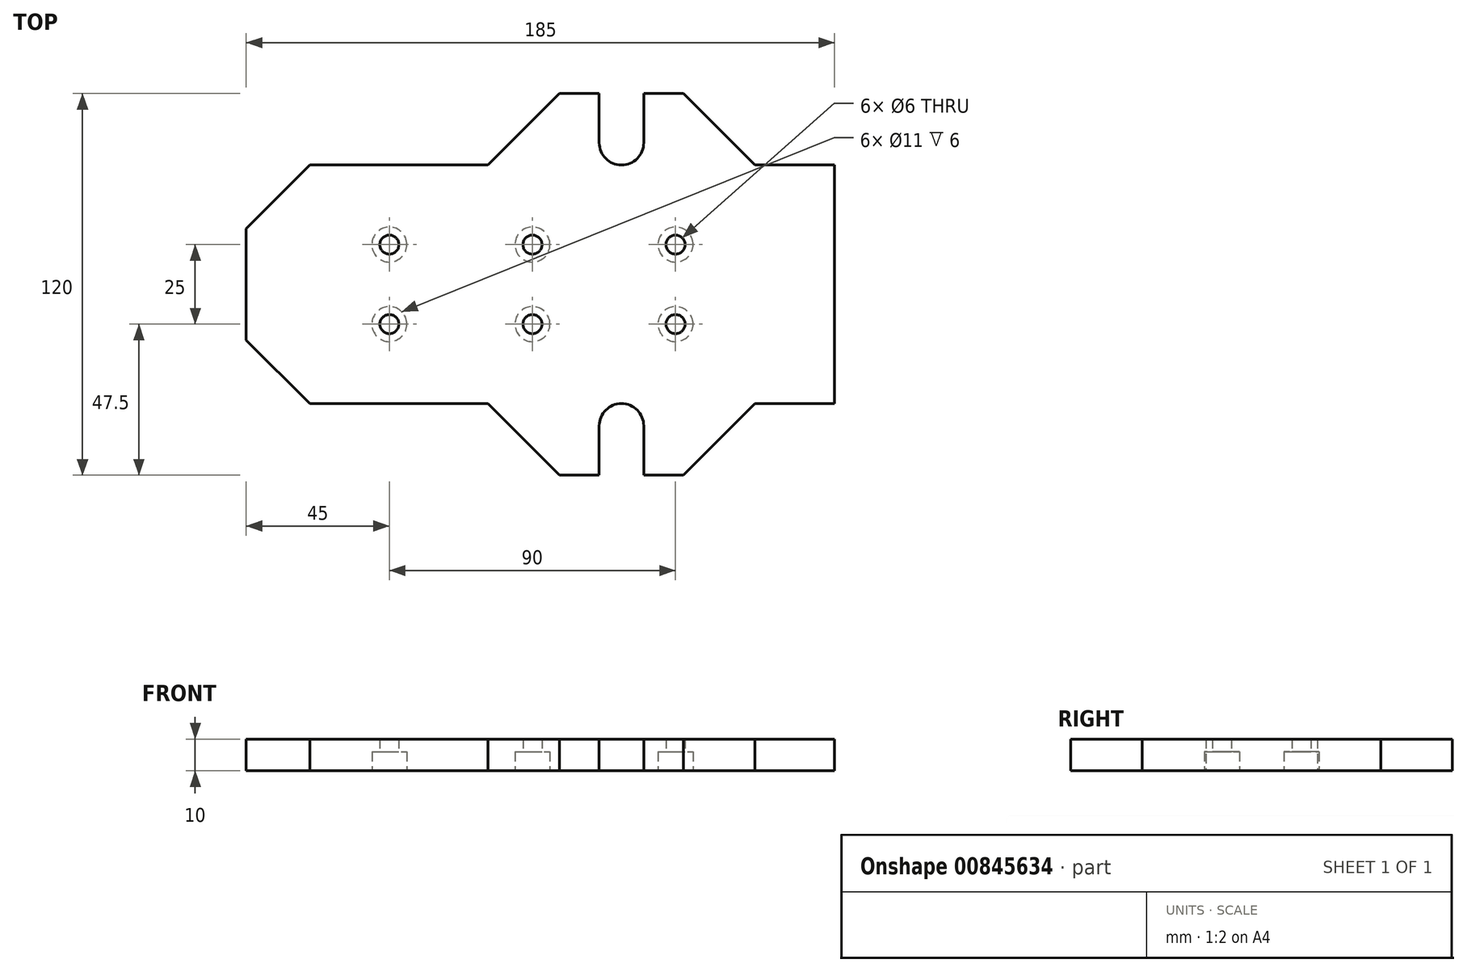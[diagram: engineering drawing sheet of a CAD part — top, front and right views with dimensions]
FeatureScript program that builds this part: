
annotation { "Feature Type Name" : "Feature", "Feature Type Description" : "" }
export const myFeature = defineFeature(function(context is Context, id is Id, definition is map)
    precondition{}
    {
        {
            var Q0;
            Q0=qCreatedBy(makeId("Top.planeOp"),FACE);
            var sketch = newSketch(context, id + "F0", { "sketchPlane" : qUnion([Q0])});
            skLineSegment(sketch, "E0", {"start": v(-118, 0) * mm, "end": v(-118, 17.5) * mm});
            skLineSegment(sketch, "E1", {"start": v(-118, 17.5) * mm, "end": v(-98, 37.5) * mm});
            skLineSegment(sketch, "E2", {"start": v(-98, 37.5) * mm, "end": v(-42, 37.5) * mm});
            skLineSegment(sketch, "E3", {"start": v(-42, 37.5) * mm, "end": v(-19.5, 60) * mm});
            skLineSegment(sketch, "E4", {"start": v(-19.5, 60) * mm, "end": v(-7, 60) * mm});
            skLineSegment(sketch, "E5", {"start": v(-7, 60) * mm, "end": v(-7, 44.5) * mm});
            skArc(sketch, "E6", {"start": v(-7, 44.5) * mm, "mid": v(0, 37.5) * mm, "end": v(7, 44.5) * mm});
            skLineSegment(sketch, "E7", {"start": v(7, 44.5) * mm, "end": v(7, 60) * mm});
            skLineSegment(sketch, "E8", {"start": v(7, 60) * mm, "end": v(19.5, 60) * mm});
            skLineSegment(sketch, "E9", {"start": v(19.5, 60) * mm, "end": v(42, 37.5) * mm});
            skLineSegment(sketch, "E10", {"start": v(42, 37.5) * mm, "end": v(67, 37.5) * mm});
            skLineSegment(sketch, "E11", {"start": v(67, 37.5) * mm, "end": v(67, 0) * mm});
            skLineSegment(sketch, "E12", {"start": v(67, 0) * mm, "end": v(-118, 0) * mm});
            skLineSegment(sketch, "E13", {"start": v(17, 12.5) * mm, "end": v(-73, 12.5) * mm, "construction": true});
            skPoint(sketch, "E14", {"position": v(-28, 12.5) * mm});
            skSolve(sketch);
        }
        {
            var Q0;
            Q0=makeQuery(id+"F0.imprint","IMPRINT",FACE,{"disambiguationData":[TD([[makeQuery(id+"F0.imprint","IMPRINT",EDGE,{"derivedFrom":sQuery(id+"F0.wireOp",EDGE,"E0")}),-1.0]])]});
            extrude(context, id + "F1", {"entities" : qUnion([Q0]), "depth" : 10 * mm, "offsetDistance" : 25 * mm});
        }
        {
            var Q0;
            Q0=sQuery(id+"F0.wireOp",VERTEX,"E13.end");
            var Q1;
            Q1=sQuery(id+"F0.wireOp",VERTEX,"E14");
            var Q2;
            Q2=sQuery(id+"F0.wireOp",VERTEX,"E13.start");
            var Q3;
            Q3=makeQuery(id+"F1.opExtrude","SWEPT_BODY",BODY,{"disambiguationData":[OSD([sQuery(id+"F0.wireOp",EDGE,"E0"),sQuery(id+"F0.wireOp",EDGE,"E1"),sQuery(id+"F0.wireOp",EDGE,"E2"),sQuery(id+"F0.wireOp",EDGE,"E3"),sQuery(id+"F0.wireOp",EDGE,"E4"),sQuery(id+"F0.wireOp",EDGE,"E5"),sQuery(id+"F0.wireOp",EDGE,"E6"),sQuery(id+"F0.wireOp",EDGE,"E7"),sQuery(id+"F0.wireOp",EDGE,"E8"),sQuery(id+"F0.wireOp",EDGE,"E9"),sQuery(id+"F0.wireOp",EDGE,"E10"),sQuery(id+"F0.wireOp",EDGE,"E11"),sQuery(id+"F0.wireOp",EDGE,"E12")])]});
            hole(context, id + "F2", {"style" : HoleStyle.C_BORE, "endStyle" : HoleEndStyle.THROUGH, "oppositeDirection" : true, "holeDiameter" : 6 * mm, "cBoreDiameter" : 11 * mm, "cBoreDepth" : 6 * mm, "majorDiameter" : 5 * mm, "isTappedThrough" : true, "tappedDepth" : 3 * mm, "tapClearance" : 3, "startFromSketch" : true, "locations" : qUnion([Q0, Q1, Q2]), "scope" : qUnion([Q3])});
        }
        {
            var Q0;
            Q0=makeQuery(id+"F1.opExtrude","SWEPT_BODY",BODY,{"disambiguationData":[OSD([sQuery(id+"F0.wireOp",EDGE,"E0"),sQuery(id+"F0.wireOp",EDGE,"E1"),sQuery(id+"F0.wireOp",EDGE,"E2"),sQuery(id+"F0.wireOp",EDGE,"E3"),sQuery(id+"F0.wireOp",EDGE,"E4"),sQuery(id+"F0.wireOp",EDGE,"E5"),sQuery(id+"F0.wireOp",EDGE,"E6"),sQuery(id+"F0.wireOp",EDGE,"E7"),sQuery(id+"F0.wireOp",EDGE,"E8"),sQuery(id+"F0.wireOp",EDGE,"E9"),sQuery(id+"F0.wireOp",EDGE,"E10"),sQuery(id+"F0.wireOp",EDGE,"E11"),sQuery(id+"F0.wireOp",EDGE,"E12")])]});
            var Q1;
            Q1=qCreatedBy(makeId("Front.planeOp"),FACE);
            mirror(context, id + "F3", {"operationType" : NewBodyOperationType.ADD, "entities" : qUnion([Q0]), "mirrorPlane" : qUnion([Q1])});
        }
    });
